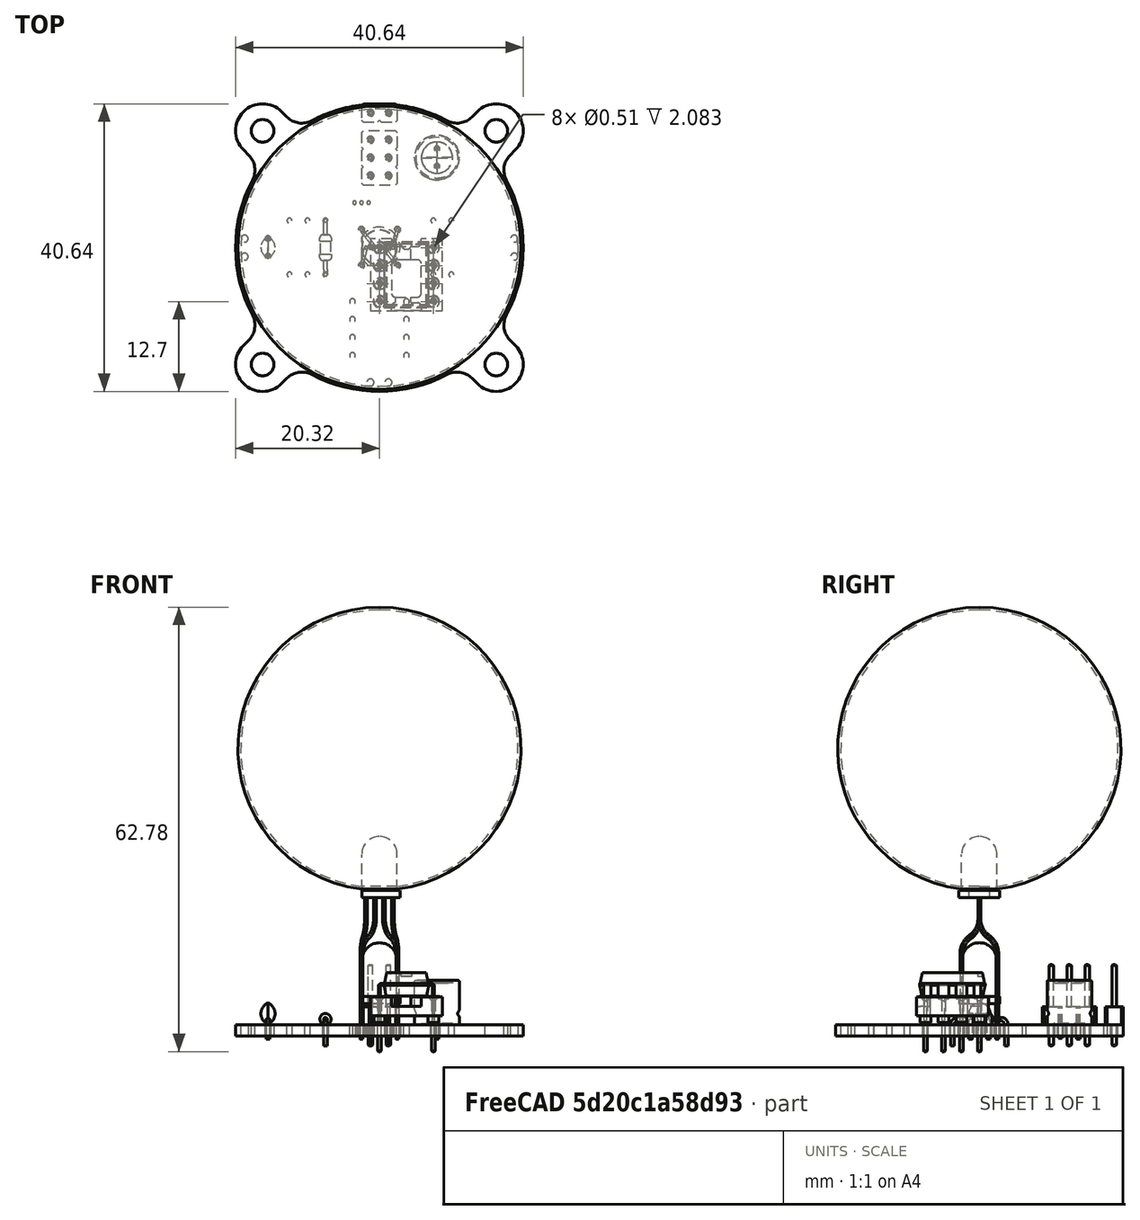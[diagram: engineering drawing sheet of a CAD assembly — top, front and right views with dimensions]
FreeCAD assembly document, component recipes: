
FREECAD ASSEMBLY — COMPONENT RECIPES ("firefly_v1_grid")

This assembly document has 2 components, labeled P0..P1 below (a component is one placed body or linked part). 1 of them carries a construction recipe — the FreeCAD feature program that regenerates the part from scratch, quoted from this document or its linked companion documents; the rest are supplied as boundary geometry only. No exploded tour is included for this assembly.
COMPONENT P0 — geometry summary ("firefly"; no construction recipe available for this part):
  bounding box: 40.6 x 40.6 x 30.4 mm
  tessellated surface: 223,748 triangles
  volume: 2649 mm^3 (5% of its bounding box)
COMPONENT P1 — recipe-attached ("Body001", modeled in this document).
Construction recipe (the document's own serialized feature program — sketch geometry with constraints, then the solid features built on it; lengths are millimeters unless a unit is written):

FEATURE [Sketcher::SketchObject] Sketch
  ArcFitTolerance = 1e-06
  AttachmentSupport = -> [XZ_Plane010]
  FullyConstrained = true
  MapMode = 5
  Placement = pos=(0,0,0) rot=(1,0,0;1.5708rad)
  Support = -> [XZ_Plane010]
  TreeRank = 12
  sketch-geometry (4):
    g0: ArcOfCircle CenterX=0 CenterY=39 CenterZ=0 NormalX=0 NormalY=0 NormalZ=1 AngleXU=0 Radius=20 StartAngle=1.5708 EndAngle=4.71239
    g1: ArcOfCircle CenterX=0 CenterY=39 CenterZ=0 NormalX=0 NormalY=0 NormalZ=1 AngleXU=0 Radius=19.6 StartAngle=1.5708 EndAngle=4.71239
    g2: LineSegment StartX=0 StartY=59 StartZ=0 EndX=0 EndY=58.6 EndZ=0
    g3: LineSegment StartX=0 StartY=19 StartZ=0 EndX=0 EndY=19.4 EndZ=0
  constraints (13):
    c: PointOnObject(g0,g-2)
    c: PointOnObject(g0,g-2)
    c: Radius(g0) = 20
    c: Coincident(g1,g0)
    c: Coincident(g2,g0)
    c: Coincident(g2,g1)
    c: Vertical(g2)
    c: Coincident(g3,g0)
    c: Coincident(g3,g1)
    c: PointOnObject(g0,g-2)
    c: Vertical(g3)
    c: DistanceY(g2,g2) = 0.4
    c: DistanceY(g-1,g0) = 39
FEATURE [PartDesign::Revolution] Revolution
  Angle = 360
  Axis = (0,-2e-16,1)
  Base = (0,0,0)
  ClaimChildren = false
  Fit = 0
  FitJoin = 0
  InnerFit = 0
  InnerFitJoin = 0
  NewSolid = false
  Placement = pos=(0,0,0) rot=(1,0,0;1.5708rad)
  Profile = -> Sketch
  ReferenceAxis = -> Sketch [V_Axis]
  Suppress = false
  TreeRank = 13
  _ProfileBasedVersion = 1
FEATURE [Sketcher::SketchObject] Sketch001
  ArcFitTolerance = 1e-06
  FullyConstrained = true
  TreeRank = 14
  sketch-geometry (1):
    g0: Circle CenterX=0 CenterY=0 CenterZ=0 NormalX=0 NormalY=0 NormalZ=1 AngleXU=0 Radius=2.5
  constraints (2):
    c: Coincident(g0,g-1)
    c: Diameter(g0) = 5
FEATURE [PartDesign::Pocket] Pocket
  BaseFeature = -> Revolution
  ClaimChildren = false
  ColoredElements = -> Pocket [Face1,Face3]
  Fit = 0
  FitJoin = 0
  InnerFit = 0
  InnerFitJoin = 0
  InnerTaperAngle = 0
  InnerTaperAngleRev = 0
  Length = 20
  Length2 = 100
  Linearize = true
  NewSolid = false
  Placement = pos=(0,0,0) rot=(1,0,0;1.5708rad)
  Profile = -> Sketch001
  Reversed = true
  Suppress = false
  TreeRank = 15
  Type = 0
  _ProfileBasedVersion = 1
FEATURE [PartDesign::Body] Body  label="Body001"
  AutoGroupSolids = false
  ClaimAllChildren = false
  ExportMode = 0
  Group = -> [Sketch,Revolution,Sketch001,Pocket]
  Origin = -> Origin010
  Tip = -> Pocket
  TreeRank = 16
  _ExportChildren = -> [Revolution,Pocket]
  _GroupVersion = 1
PROVENANCE & LICENSES
A FreeCAD (.FCStd) document from a public repository crawl; recipes are the document's own serialized feature recipes (and, for linked parts, companion documents' recipes).
License: gpl-3.0.
